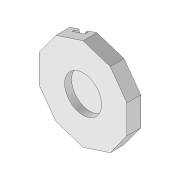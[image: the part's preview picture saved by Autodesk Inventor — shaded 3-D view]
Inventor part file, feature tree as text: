
AUTODESK INVENTOR PART (.ipt)
format: ipt  version: 2020 (Build 240168000, 168)  size: 123,904 bytes
history: native  units: mm
features: extrude x3, sketch x3, projected_geometry x1
ambient origin geometry x8: Origin, YZ Plane, XZ Plane, XY Plane, X Axis, Y Axis, Z Axis, Center Point
bodies: Volumenkörper1 (feature_tree)
feature tree (7):
  extrude  "Extrusion1"  Depth=100.0mm
  extrude  "Extrusion2"  Depth=15.0mm TaperAngle=0.0deg
  extrude  "Extrusion3"  Depth=10.0mm
  sketch  "Skizze1"  dims[d0=80.0mm d1=100.0mm]
  sketch  "Skizze3"  dims[d2=15.0mm d3=0.0mm d4=15.0mm d5=0.0mm]
  projected_geometry  "Projizierte Kontur1"
  sketch  "Skizze4"  dims[d6=20.0mm d7=10.0mm d8=30.0mm d9=15.0mm d10=5.0mm d11=5.0mm d12=0.0mm d13=0.0mm]
